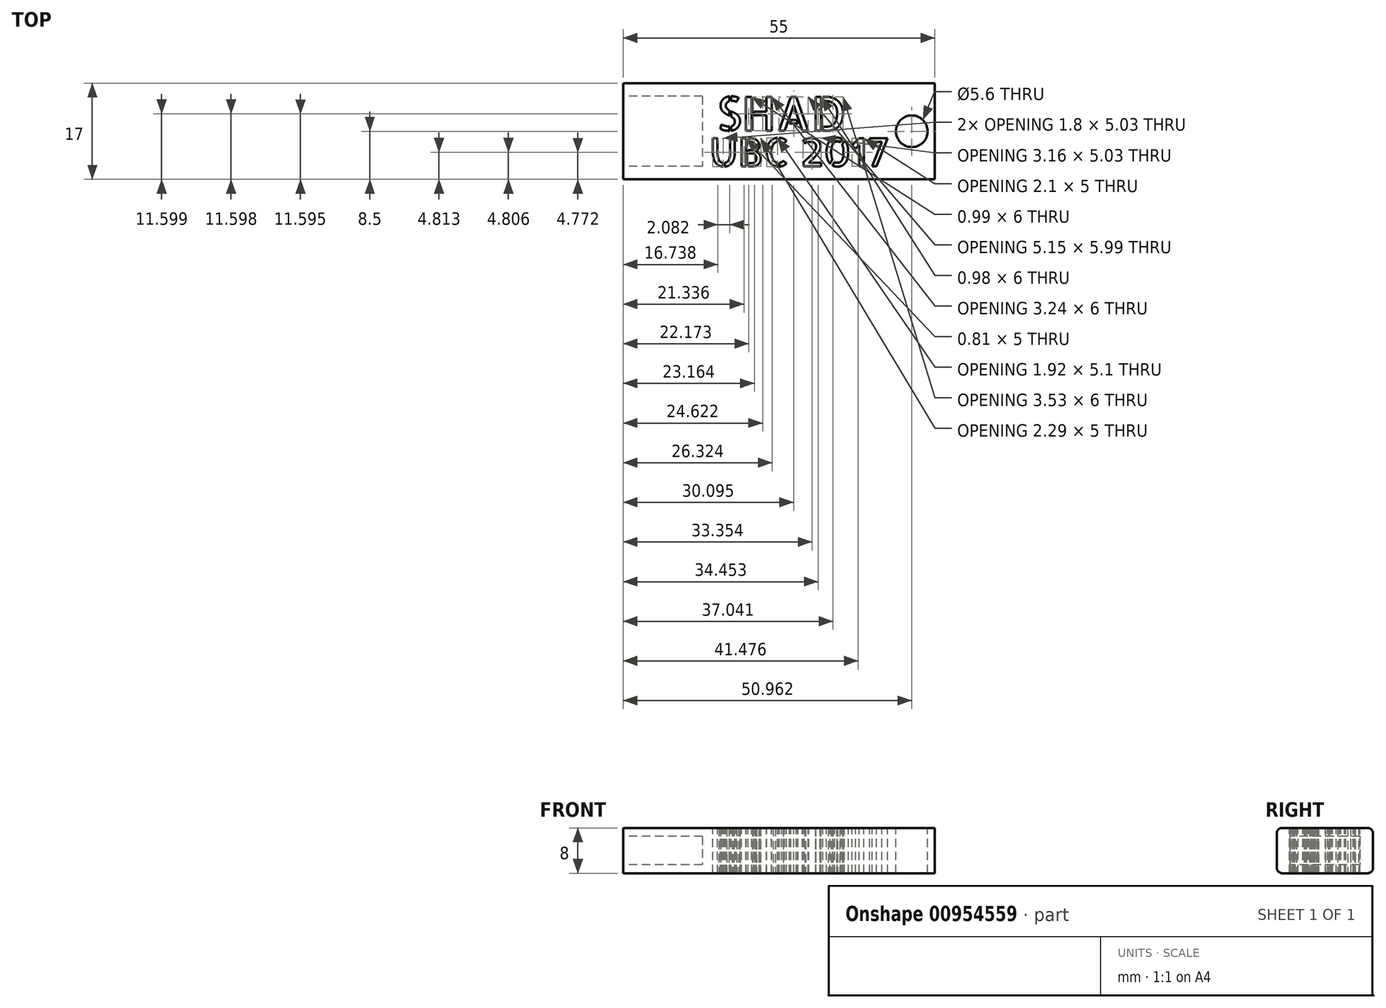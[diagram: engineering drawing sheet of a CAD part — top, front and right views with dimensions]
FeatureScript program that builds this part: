
annotation { "Feature Type Name" : "Feature", "Feature Type Description" : "" }
export const myFeature = defineFeature(function(context is Context, id is Id, definition is map)
    precondition{}
    {
        {
            var Q0;
            Q0=qCreatedBy(makeId("Front.planeOp"),FACE);
            var sketch = newSketch(context, id + "F0", { "sketchPlane" : qUnion([Q0])});
            skLineSegment(sketch, "E0.bottom", {"start": v(-7.5, 4) * mm, "end": v(7.5, 4) * mm});
            skLineSegment(sketch, "E0.top", {"start": v(-7.5, -4) * mm, "end": v(7.5, -4) * mm});
            skLineSegment(sketch, "E0.left", {"start": v(-8.5, 3) * mm, "end": v(-8.5, -3) * mm});
            skLineSegment(sketch, "E0.right", {"start": v(8.5, 3) * mm, "end": v(8.5, -3) * mm});
            skPoint(sketch, "E0.middle", {"position": v(0, 0) * mm});
            skPoint(sketch, "E1.visualSharp", {"position": v(-8.5, 4) * mm});
            skArc(sketch, "E1.filletArc", {"start": v(-7.5, 4) * mm, "mid": v(-8.2, 3.7) * mm, "end": v(-8.5, 3) * mm});
            skPoint(sketch, "E2.visualSharp", {"position": v(-8.5, -4) * mm});
            skArc(sketch, "E2.filletArc", {"start": v(-8.5, -3) * mm, "mid": v(-8.2, -3.7) * mm, "end": v(-7.5, -4) * mm});
            skPoint(sketch, "E3.visualSharp", {"position": v(8.5, 4) * mm});
            skArc(sketch, "E3.filletArc", {"start": v(8.5, 3) * mm, "mid": v(8.2, 3.7) * mm, "end": v(7.5, 4) * mm});
            skPoint(sketch, "E4.visualSharp", {"position": v(8.5, -4) * mm});
            skArc(sketch, "E4.filletArc", {"start": v(7.5, -4) * mm, "mid": v(8.2, -3.7) * mm, "end": v(8.5, -3) * mm});
            skSolve(sketch);
        }
        {
            var Q0;
            Q0 = qSketchRegion(id + "F0", true);
            extrude(context, id + "F1", {"entities" : qUnion([Q0]), "depth" : 55 * mm, "offsetDistance" : 25 * mm});
        }
        {
            var Q0;
            Q0=makeQuery(id+"F1.opExtrude","CAP_FACE",FACE,{"disambiguationData":[OSD([sQuery(id+"F0.wireOp",EDGE,"E0.bottom"),sQuery(id+"F0.wireOp",EDGE,"E0.top"),sQuery(id+"F0.wireOp",EDGE,"E0.left"),sQuery(id+"F0.wireOp",EDGE,"E0.right"),sQuery(id+"F0.wireOp",EDGE,"E1.filletArc"),sQuery(id+"F0.wireOp",EDGE,"E2.filletArc"),sQuery(id+"F0.wireOp",EDGE,"E3.filletArc"),sQuery(id+"F0.wireOp",EDGE,"E4.filletArc")])],"isStart":false});
            var sketch = newSketch(context, id + "F2", { "sketchPlane" : qUnion([Q0])});
            skLineSegment(sketch, "E5.bottom", {"start": v(-6.2, 2.5) * mm, "end": v(6.2, 2.5) * mm});
            skLineSegment(sketch, "E5.top", {"start": v(-6.2, -2.5) * mm, "end": v(6.2, -2.5) * mm});
            skLineSegment(sketch, "E5.left", {"start": v(-6.2, 2.5) * mm, "end": v(-6.2, -2.5) * mm});
            skLineSegment(sketch, "E5.right", {"start": v(6.2, 2.5) * mm, "end": v(6.2, -2.5) * mm});
            skPoint(sketch, "E5.middle", {"position": v(0, 0) * mm});
            skSolve(sketch);
        }
        {
            var Q0;
            Q0 = qSketchRegion(id + "F2", true);
            extrude(context, id + "F3", {"entities" : qUnion([Q0]), "operationType" : NewBodyOperationType.REMOVE, "oppositeDirection" : true, "depth" : 14 * mm, "offsetDistance" : 25 * mm});
        }
        {
            var Q0;
            Q0=makeQuery(id+"F1.opExtrude","SWEPT_BODY",BODY,{"disambiguationData":[OSD([sQuery(id+"F0.wireOp",EDGE,"E0.bottom"),sQuery(id+"F0.wireOp",EDGE,"E0.top"),sQuery(id+"F0.wireOp",EDGE,"E0.left"),sQuery(id+"F0.wireOp",EDGE,"E0.right"),sQuery(id+"F0.wireOp",EDGE,"E1.filletArc"),sQuery(id+"F0.wireOp",EDGE,"E2.filletArc"),sQuery(id+"F0.wireOp",EDGE,"E3.filletArc"),sQuery(id+"F0.wireOp",EDGE,"E4.filletArc")])]});
            var Q1;
            Q1=makeQuery(id+"F1.opExtrude","CAP_EDGE",EDGE,{"disambiguationData":[OSD([sQuery(id+"F0.wireOp",EDGE,"E0.right")])],"isStart":true});
            transform(context, id + "F4", {"entities" : qUnion([Q0]), "transformType" : TransformType.ROTATION, "transformAxis" : qUnion([Q1]), "angle" : 90 * degree, "makeCopy" : false});
        }
        {
            var Q0;
            Q0=makeQuery(id+"F1.opExtrude","SWEPT_FACE",FACE,{"disambiguationData":[OSD([sQuery(id+"F0.wireOp",EDGE,"E0.bottom")])]});
            var sketch = newSketch(context, id + "F5", { "sketchPlane" : qUnion([Q0])});
            skText(sketch, "E6", { "text": "SHAD", "fontName": "AllertaStencil-Regular.ttf"});
            skText(sketch, "E7", { "text": "UBC 2017\n", "fontName": "AllertaStencil-Regular.ttf"});
            const initialGuessF5  = {"E6": [-0.03, 0.0086, 1, 0, 0.006], "E7": [-0.03122, 0.00229, 1, 0, 0.005]};
            skSetInitialGuess(sketch, initialGuessF5);
            skSolve(sketch);
        }
        {
            var Q0;
            Q0 = qSketchRegion(id + "F5", true);
            extrude(context, id + "F6", {"entities" : qUnion([Q0]), "operationType" : NewBodyOperationType.REMOVE, "oppositeDirection" : true, "depth" : 8 * mm, "offsetDistance" : 25 * mm});
        }
        {
            var Q0;
            Q0=makeQuery(id+"F1.opExtrude","SWEPT_FACE",FACE,{"disambiguationData":[OSD([sQuery(id+"F0.wireOp",EDGE,"E0.bottom")])]});
            var sketch = newSketch(context, id + "F7", { "sketchPlane" : qUnion([Q0])});
            skCircle(sketch, "E8", {"center": v(4.46, 8.5) * mm, "radius": 2.8 * mm});
            skPoint(sketch, "E8.centerSnap0", {"position": v(8.5, 8.5) * mm});
            skSolve(sketch);
        }
        {
            var Q0;
            Q0=makeQuery(id+"F7.imprint","IMPRINT",FACE,{"disambiguationData":[TD([[makeQuery(id+"F7.imprint","IMPRINT",EDGE,{"derivedFrom":sQuery(id+"F7.wireOp",EDGE,"E8")}),1.0]])]});
            extrude(context, id + "F8", {"entities" : qUnion([Q0]), "operationType" : NewBodyOperationType.REMOVE, "oppositeDirection" : true, "depth" : 25 * mm, "offsetDistance" : 25 * mm});
        }
    });
